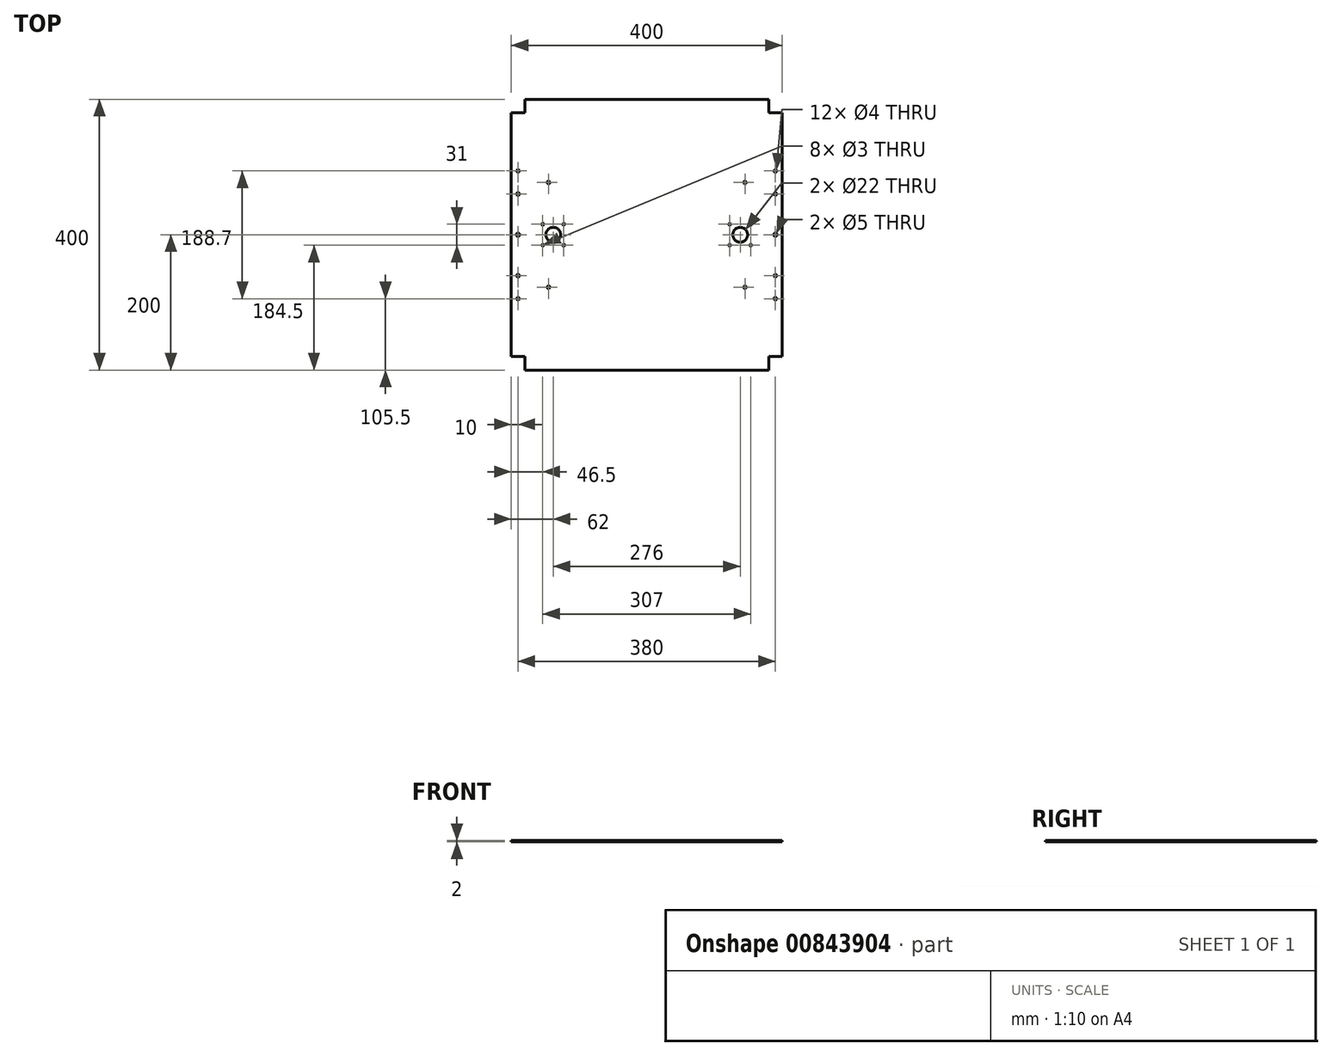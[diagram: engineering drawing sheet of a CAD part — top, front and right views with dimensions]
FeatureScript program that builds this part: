
annotation { "Feature Type Name" : "Feature", "Feature Type Description" : "" }
export const myFeature = defineFeature(function(context is Context, id is Id, definition is map)
    precondition{}
    {
        {
            var Q0;
            Q0=qCreatedBy(makeId("Top.planeOp"),FACE);
            var sketch = newSketch(context, id + "F0", { "sketchPlane" : qUnion([Q0])});
            skLineSegment(sketch, "E0.0", {"start": v(200, 180) * mm, "end": v(200, -180) * mm});
            skLineSegment(sketch, "E0.1", {"start": v(180, -200) * mm, "end": v(-180, -200) * mm});
            skLineSegment(sketch, "E0.2", {"start": v(-200, -180) * mm, "end": v(-200, 180) * mm});
            skLineSegment(sketch, "E0.3", {"start": v(-180, 200) * mm, "end": v(180, 200) * mm});
            skPoint(sketch, "E0.0.midPoint", {"position": v(200, 0) * mm});
            skLineSegment(sketch, "E1.right", {"start": v(-180, 200) * mm, "end": v(-180, 180) * mm});
            skLineSegment(sketch, "E2.top", {"start": v(200, 180) * mm, "end": v(180, 180) * mm});
            skLineSegment(sketch, "E2.right", {"start": v(180, 200) * mm, "end": v(180, 180) * mm});
            skLineSegment(sketch, "E3.top", {"start": v(200, -180) * mm, "end": v(180, -180) * mm});
            skLineSegment(sketch, "E3.right", {"start": v(180, -200) * mm, "end": v(180, -180) * mm});
            skLineSegment(sketch, "E4.right", {"start": v(-180, -200) * mm, "end": v(-180, -180) * mm});
            skLineSegment(sketch, "E5", {"start": v(209.47, 0) * mm, "end": v(-258.55, 0) * mm, "construction": true});
            skCircle(sketch, "E6", {"center": v(-138, 0) * mm, "radius": 11 * mm});
            skCircle(sketch, "E7", {"center": v(-153.5, 15.5) * mm, "radius": 1.5 * mm});
            skCircle(sketch, "E8", {"center": v(-122.5, 15.5) * mm, "radius": 1.5 * mm});
            skCircle(sketch, "E9", {"center": v(-122.5, -15.5) * mm, "radius": 1.5 * mm});
            skCircle(sketch, "E10", {"center": v(-153.5, -15.5) * mm, "radius": 1.5 * mm});
            skCircle(sketch, "E11", {"center": v(-190, 0) * mm, "radius": 2.5 * mm});
            skCircle(sketch, "E12.MirrorC", {"center": v(153.5, 15.5) * mm, "radius": 1.5 * mm});
            skCircle(sketch, "E13.MirrorC", {"center": v(153.5, -15.5) * mm, "radius": 1.5 * mm});
            skCircle(sketch, "E14.MirrorC", {"center": v(122.5, -15.5) * mm, "radius": 1.5 * mm});
            skCircle(sketch, "E15.MirrorC", {"center": v(138, 0) * mm, "radius": 11 * mm});
            skCircle(sketch, "E16.MirrorC", {"center": v(122.5, 15.5) * mm, "radius": 1.5 * mm});
            skCircle(sketch, "E17.MirrorC", {"center": v(190, 0) * mm, "radius": 2.5 * mm});
            skCircle(sketch, "E18", {"center": v(-170, -77.5) * mm, "radius": 4 * mm, "construction": true});
            skCircle(sketch, "E19", {"center": v(-170, -77.5) * mm, "radius": 8 * mm, "construction": true});
            skCircle(sketch, "E20", {"center": v(-190, -60.5) * mm, "radius": 2 * mm});
            skCircle(sketch, "E21", {"center": v(-190, -94.5) * mm, "radius": 2 * mm});
            skCircle(sketch, "E22", {"center": v(-145, -77.5) * mm, "radius": 2 * mm});
            skLineSegment(sketch, "E23.top", {"start": v(-178.98, -47.5) * mm, "end": v(-200, -47.5) * mm, "construction": true});
            skLineSegment(sketch, "E23.right", {"start": v(-200, -107.5) * mm, "end": v(-200, -47.5) * mm, "construction": true});
            skPoint(sketch, "E24", {"position": v(-200, -77.5) * mm});
            skLineSegment(sketch, "E25", {"start": v(-178.98, -47.5) * mm, "end": v(-178.98, -107.5) * mm, "construction": true});
            skArc(sketch, "E26", {"start": v(-139.72, -88.28) * mm, "mid": v(-133, -77.5) * mm, "end": v(-139.72, -66.72) * mm, "construction": true});
            skLineSegment(sketch, "E27", {"start": v(-178.98, -47.5) * mm, "end": v(-139.72, -66.72) * mm, "construction": true});
            skLineSegment(sketch, "E28", {"start": v(-178.98, -107.5) * mm, "end": v(-139.72, -88.28) * mm, "construction": true});
            skCircle(sketch, "E29", {"center": v(-170, 77.5) * mm, "radius": 4 * mm, "construction": true});
            skCircle(sketch, "E30", {"center": v(-170, 77.5) * mm, "radius": 8 * mm, "construction": true});
            skCircle(sketch, "E31", {"center": v(-190, 94.2) * mm, "radius": 2 * mm});
            skCircle(sketch, "E32", {"center": v(-190, 60.2) * mm, "radius": 2 * mm});
            skCircle(sketch, "E33", {"center": v(-145, 77.2) * mm, "radius": 2 * mm});
            skLineSegment(sketch, "E34.bottom", {"start": v(-178.98, 47.2) * mm, "end": v(-200, 47.2) * mm, "construction": true});
            skLineSegment(sketch, "E34.right", {"start": v(-200, 47.2) * mm, "end": v(-200, 107.2) * mm, "construction": true});
            skLineSegment(sketch, "E35", {"start": v(-178.98, 107.2) * mm, "end": v(-178.98, 47.2) * mm, "construction": true});
            skArc(sketch, "E36", {"start": v(-139.72, 66.42) * mm, "mid": v(-133, 77.2) * mm, "end": v(-139.72, 87.98) * mm, "construction": true});
            skLineSegment(sketch, "E37", {"start": v(-178.98, 107.2) * mm, "end": v(-139.72, 87.98) * mm, "construction": true});
            skLineSegment(sketch, "E38", {"start": v(-178.98, 47.2) * mm, "end": v(-139.72, 66.42) * mm, "construction": true});
            skLineSegment(sketch, "E39", {"start": v(-200, 180) * mm, "end": v(-180, 180) * mm});
            skLineSegment(sketch, "E40", {"start": v(-200, 107.2) * mm, "end": v(-178.98, 107.2) * mm, "construction": true});
            skLineSegment(sketch, "E41", {"start": v(-200, -180) * mm, "end": v(-180, -180) * mm});
            skLineSegment(sketch, "E42", {"start": v(-200, -107.5) * mm, "end": v(-178.98, -107.5) * mm, "construction": true});
            skCircle(sketch, "E43.MirrorC", {"center": v(145, -77.5) * mm, "radius": 2 * mm});
            skLineSegment(sketch, "E44.MirrorCS", {"start": v(200, -107.5) * mm, "end": v(178.98, -107.5) * mm, "construction": true});
            skCircle(sketch, "E45.MirrorC", {"center": v(170, -77.5) * mm, "radius": 4 * mm, "construction": true});
            skLineSegment(sketch, "E46.MirrorCS", {"start": v(178.98, -47.5) * mm, "end": v(200, -47.5) * mm, "construction": true});
            skCircle(sketch, "E47.MirrorC", {"center": v(190, -94.5) * mm, "radius": 2 * mm});
            skArc(sketch, "E48.MirrorCS", {"start": v(139.72, -88.28) * mm, "mid": v(133, -77.5) * mm, "end": v(139.72, -66.72) * mm, "construction": true});
            skCircle(sketch, "E49.MirrorC", {"center": v(170, -77.5) * mm, "radius": 8 * mm, "construction": true});
            skCircle(sketch, "E50.MirrorC", {"center": v(190, -60.5) * mm, "radius": 2 * mm});
            skLineSegment(sketch, "E51.MirrorCS", {"start": v(178.98, -47.5) * mm, "end": v(178.98, -107.5) * mm, "construction": true});
            skLineSegment(sketch, "E52.MirrorCS", {"start": v(200, -107.5) * mm, "end": v(200, -47.5) * mm, "construction": true});
            skLineSegment(sketch, "E53.MirrorCS", {"start": v(178.98, -107.5) * mm, "end": v(139.72, -88.28) * mm, "construction": true});
            skLineSegment(sketch, "E54.MirrorCS", {"start": v(178.98, -47.5) * mm, "end": v(139.72, -66.72) * mm, "construction": true});
            skPoint(sketch, "E55.MirrorP", {"position": v(200, -77.5) * mm});
            skCircle(sketch, "E56.MirrorC", {"center": v(190, 60.2) * mm, "radius": 2 * mm});
            skCircle(sketch, "E57.MirrorC", {"center": v(190, 94.2) * mm, "radius": 2 * mm});
            skCircle(sketch, "E58.MirrorC", {"center": v(170, 77.5) * mm, "radius": 4 * mm, "construction": true});
            skCircle(sketch, "E59.MirrorC", {"center": v(145, 77.2) * mm, "radius": 2 * mm});
            skLineSegment(sketch, "E60.MirrorCS", {"start": v(178.98, 47.2) * mm, "end": v(200, 47.2) * mm, "construction": true});
            skLineSegment(sketch, "E61.MirrorCS", {"start": v(200, 107.2) * mm, "end": v(178.98, 107.2) * mm, "construction": true});
            skLineSegment(sketch, "E62.MirrorCS", {"start": v(200, 47.2) * mm, "end": v(200, 107.2) * mm, "construction": true});
            skLineSegment(sketch, "E63.MirrorCS", {"start": v(178.98, 107.2) * mm, "end": v(178.98, 47.2) * mm, "construction": true});
            skCircle(sketch, "E64.MirrorC", {"center": v(170, 77.5) * mm, "radius": 8 * mm, "construction": true});
            skLineSegment(sketch, "E65.MirrorCS", {"start": v(178.98, 47.2) * mm, "end": v(139.72, 66.42) * mm, "construction": true});
            skLineSegment(sketch, "E66.MirrorCS", {"start": v(178.98, 107.2) * mm, "end": v(139.72, 87.98) * mm, "construction": true});
            skArc(sketch, "E67.MirrorCS", {"start": v(139.72, 66.42) * mm, "mid": v(133, 77.2) * mm, "end": v(139.72, 87.98) * mm, "construction": true});
            skSolve(sketch);
        }
        {
            var Q0;
            Q0=makeQuery(id+"F0.imprint","IMPRINT",FACE,{"disambiguationData":[TD([[makeQuery(id+"F0.imprint","IMPRINT",EDGE,{"derivedFrom":sQuery(id+"F0.wireOp",EDGE,"E0.0")}),-1.0]])]});
            extrude(context, id + "F1", {"entities" : qUnion([Q0]), "oppositeDirection" : true, "depth" : 2 * mm, "offsetDistance" : 25 * mm});
        }
    });
